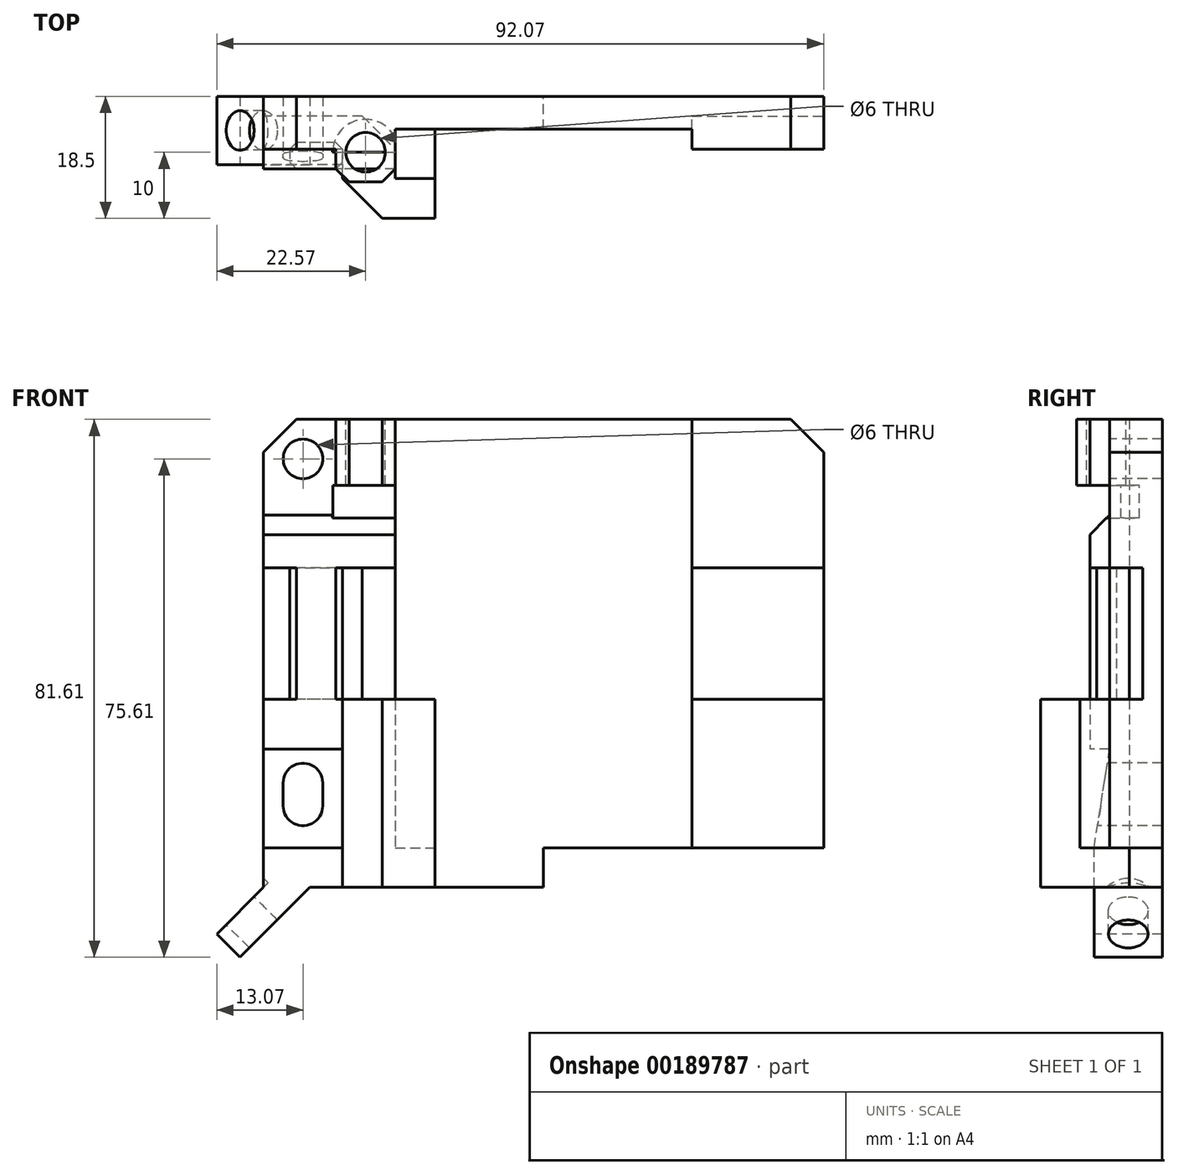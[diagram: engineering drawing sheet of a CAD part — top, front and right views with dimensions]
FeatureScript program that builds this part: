
annotation { "Feature Type Name" : "Feature", "Feature Type Description" : "" }
export const myFeature = defineFeature(function(context is Context, id is Id, definition is map)
    precondition{}
    {
        {
            var Q0;
            Q0=qCreatedBy(makeId("Front.planeOp"),FACE);
            var sketch = newSketch(context, id + "F0", { "sketchPlane" : qUnion([Q0])});
            skLineSegment(sketch, "E0.bottom", {"start": v(42.5, -32.5) * mm, "end": v(-42.5, -32.5) * mm});
            skLineSegment(sketch, "E0.top", {"start": v(42.5, 32.5) * mm, "end": v(-42.5, 32.5) * mm});
            skLineSegment(sketch, "E0.left", {"start": v(42.5, -32.5) * mm, "end": v(42.5, 32.5) * mm});
            skLineSegment(sketch, "E0.right", {"start": v(-42.5, -32.5) * mm, "end": v(-42.5, 32.5) * mm});
            skPoint(sketch, "E0.middle", {"position": v(0, 0) * mm});
            skSolve(sketch);
        }
        {
            var Q0;
            Q0 = qSketchRegion(id + "F0", true);
            extrude(context, id + "F1", {"entities" : qUnion([Q0]), "depth" : 8 * mm});
        }
        {
            var Q0;
            Q0=makeQuery(id+"F1.opExtrude","SWEPT_FACE",FACE,{"disambiguationData":[OSD([sQuery(id+"F0.wireOp",EDGE,"E0.right")])]});
            var sketch = newSketch(context, id + "F2", { "sketchPlane" : qUnion([Q0])});
            skLineSegment(sketch, "E1", {"start": v(8, -32.5) * mm, "end": v(10.38, -32.5) * mm});
            skLineSegment(sketch, "E2", {"start": v(10.38, -32.5) * mm, "end": v(8, -17.5) * mm});
            skLineSegment(sketch, "E3", {"start": v(8, -17.5) * mm, "end": v(8, -32.5) * mm});
            skSolve(sketch);
        }
        {
            var Q0;
            Q0=makeQuery(id+"F1.opExtrude","CAP_FACE",FACE,{"disambiguationData":[OSD([sQuery(id+"F0.wireOp",EDGE,"E0.bottom"),sQuery(id+"F0.wireOp",EDGE,"E0.top"),sQuery(id+"F0.wireOp",EDGE,"E0.left"),sQuery(id+"F0.wireOp",EDGE,"E0.right")])],"isStart":false});
            var sketch = newSketch(context, id + "F3", { "sketchPlane" : qUnion([Q0])});
            skLineSegment(sketch, "E4", {"start": v(-42.5, 26.5) * mm, "end": v(42.5, 26.5) * mm, "construction": true});
            skCircle(sketch, "E5", {"center": v(-36.5, 26.5) * mm, "radius": 3 * mm});
            skLineSegment(sketch, "E6", {"start": v(-36.5, 26.5) * mm, "end": v(-36.5, -32.5) * mm, "construction": true});
            skArc(sketch, "E7", {"start": v(-33.5, -22.65) * mm, "mid": v(-36.5, -19.65) * mm, "end": v(-39.5, -22.65) * mm});
            skArc(sketch, "E8", {"start": v(-39.5, -26.15) * mm, "mid": v(-36.5, -29.15) * mm, "end": v(-33.5, -26.15) * mm});
            skLineSegment(sketch, "E9", {"start": v(-39.5, -26.15) * mm, "end": v(-39.5, -22.65) * mm});
            skLineSegment(sketch, "E10", {"start": v(-33.5, -22.65) * mm, "end": v(-33.5, -26.15) * mm});
            skSolve(sketch);
        }
        {
            var Q0;
            Q0 = qSketchRegion(id + "F2", true);
            extrude(context, id + "F4", {"entities" : qUnion([Q0]), "operationType" : NewBodyOperationType.ADD, "oppositeDirection" : true, "depth" : 12 * mm});
        }
        {
            var Q0;
            Q0 = qSketchRegion(id + "F3", true);
            extrude(context, id + "F5", {"entities" : qUnion([Q0]), "operationType" : NewBodyOperationType.REMOVE, "endBound" : BoundingType.SYMMETRIC, "oppositeDirection" : true, "depth" : 50 * mm});
        }
        {
            var Q0;
            Q0=makeQuery(id+"F1.opExtrude","CAP_FACE",FACE,{"disambiguationData":[OSD([sQuery(id+"F0.wireOp",EDGE,"E0.bottom"),sQuery(id+"F0.wireOp",EDGE,"E0.top"),sQuery(id+"F0.wireOp",EDGE,"E0.left"),sQuery(id+"F0.wireOp",EDGE,"E0.right")])],"isStart":false});
            var sketch = newSketch(context, id + "F6", { "sketchPlane" : qUnion([Q0])});
            skLineSegment(sketch, "E11", {"start": v(-42.5, 10) * mm, "end": v(42.5, 10) * mm});
            skLineSegment(sketch, "E12", {"start": v(42.5, 10) * mm, "end": v(42.5, -10) * mm});
            skLineSegment(sketch, "E13", {"start": v(42.5, -10) * mm, "end": v(-42.5, -10) * mm});
            skLineSegment(sketch, "E14", {"start": v(-42.5, -10) * mm, "end": v(-42.5, 10) * mm});
            skSolve(sketch);
        }
        {
            var Q0;
            Q0 = qSketchRegion(id + "F6", true);
            extrude(context, id + "F7", {"entities" : qUnion([Q0]), "operationType" : NewBodyOperationType.REMOVE, "oppositeDirection" : true, "depth" : 5 * mm});
        }
        {
            var Q0;
            {var subQ0=sQuery(id+"F2.wireOp",EDGE,"E1");Q0=makeQuery(id+"FlQiG0HdQTh74tr_1.1.F4.boolean.opBoolean","MERGE",FACE,{"derivedFrom":[makeQuery(id+"F4.boolean.opBoolean","MERGE",FACE,{"derivedFrom":[makeQuery(id+"F1.opExtrude","SWEPT_FACE",FACE,{"disambiguationData":[OSD([sQuery(id+"F0.wireOp",EDGE,"E0.bottom")])]}),makeQuery(id+"F4.opExtrude","SWEPT_FACE",FACE,{"disambiguationData":[OSD([subQ0])]})]}),makeQuery(id+"FlQiG0HdQTh74tr_1.1.F4.opExtrude","SWEPT_FACE",FACE,{"disambiguationData":[OSD([subQ0])]})]});}
            var sketch = newSketch(context, id + "F8", { "sketchPlane" : qUnion([Q0])});
            skLineSegment(sketch, "E15", {"start": v(-22.5, 8) * mm, "end": v(-22.5, 12.5) * mm});
            skLineSegment(sketch, "E16", {"start": v(-22.5, 12.5) * mm, "end": v(-16.5, 12.5) * mm});
            skLineSegment(sketch, "E17", {"start": v(-16.5, 12.5) * mm, "end": v(-16.5, 18.5) * mm});
            skLineSegment(sketch, "E18", {"start": v(-16.5, 18.5) * mm, "end": v(-30.5, 18.5) * mm});
            skLineSegment(sketch, "E19", {"start": v(-30.5, 18.5) * mm, "end": v(-30.5, 8) * mm});
            skLineSegment(sketch, "E20", {"start": v(-30.5, 8) * mm, "end": v(-22.5, 8) * mm});
            skSolve(sketch);
        }
        {
            var Q0;
            Q0 = qSketchRegion(id + "F8", true);
            extrude(context, id + "F9", {"entities" : qUnion([Q0]), "operationType" : NewBodyOperationType.ADD, "oppositeDirection" : true, "depth" : 22.5 * mm});
        }
        {
            var Q0;
            Q0=makeQuery(id+"F9.opExtrude","SWEPT_EDGE",EDGE,{"disambiguationData":[OSD([sQuery(id+"F8.wireOp",EDGE,"E18"),sQuery(id+"F8.wireOp",EDGE,"E19")])]});
            chamfer(context, id + "F10", {"entities" : qUnion([Q0]), "width" : 6 * mm, "tangentPropagation" : true});
        }
        {
            var Q0;
            {var subQ0=sQuery(id+"F2.wireOp",EDGE,"E1");Q0=makeQuery(id+"F9.boolean.opBoolean","MERGE",FACE,{"derivedFrom":[makeQuery(id+"FlQiG0HdQTh74tr_1.1.F4.boolean.opBoolean","MERGE",FACE,{"derivedFrom":[makeQuery(id+"F4.boolean.opBoolean","MERGE",FACE,{"derivedFrom":[makeQuery(id+"F1.opExtrude","SWEPT_FACE",FACE,{"disambiguationData":[OSD([sQuery(id+"F0.wireOp",EDGE,"E0.bottom")])]}),makeQuery(id+"F4.opExtrude","SWEPT_FACE",FACE,{"disambiguationData":[OSD([subQ0])]})]}),makeQuery(id+"FlQiG0HdQTh74tr_1.1.F4.opExtrude","SWEPT_FACE",FACE,{"disambiguationData":[OSD([subQ0])]})]}),makeQuery(id+"F9.opExtrude","CAP_FACE",FACE,{"disambiguationData":[OSD([sQuery(id+"F8.wireOp",EDGE,"E15"),sQuery(id+"F8.wireOp",EDGE,"E16"),sQuery(id+"F8.wireOp",EDGE,"E17"),sQuery(id+"F8.wireOp",EDGE,"E18"),sQuery(id+"F8.wireOp",EDGE,"E19"),sQuery(id+"F8.wireOp",EDGE,"E20")])],"isStart":true})]});}
            var sketch = newSketch(context, id + "F11", { "sketchPlane" : qUnion([Q0])});
            skLineSegment(sketch, "E21", {"start": v(0, 0) * mm, "end": v(-42.5, 0) * mm});
            skLineSegment(sketch, "E22", {"start": v(-42.5, 0) * mm, "end": v(-42.5, 10.38) * mm});
            skLineSegment(sketch, "E23", {"start": v(-42.5, 10.38) * mm, "end": v(-30.5, 10.38) * mm});
            skLineSegment(sketch, "E24", {"start": v(-30.5, 10.38) * mm, "end": v(-30.5, 12.5) * mm});
            skLineSegment(sketch, "E25", {"start": v(-30.5, 12.5) * mm, "end": v(-24.5, 18.5) * mm});
            skLineSegment(sketch, "E26", {"start": v(-24.5, 18.5) * mm, "end": v(-16.5, 18.5) * mm});
            skLineSegment(sketch, "E27", {"start": v(-16.5, 18.5) * mm, "end": v(-16.5, 8) * mm});
            skLineSegment(sketch, "E28", {"start": v(-16.5, 8) * mm, "end": v(0, 8) * mm});
            skLineSegment(sketch, "E29", {"start": v(0, 8) * mm, "end": v(0, 0) * mm});
            skSolve(sketch);
        }
        {
            var Q0;
            Q0 = qSketchRegion(id + "F11", true);
            extrude(context, id + "F12", {"entities" : qUnion([Q0]), "operationType" : NewBodyOperationType.ADD, "depth" : 6 * mm});
        }
        {
            var Q0;
            Q0=makeQuery(id+"F12.opExtrude","SWEPT_FACE",FACE,{"disambiguationData":[OSD([sQuery(id+"F11.wireOp",EDGE,"E23")])]});
            var sketch = newSketch(context, id + "F13", { "sketchPlane" : qUnion([Q0])});
            skLineSegment(sketch, "E30", {"start": v(-42.5, -38.5) * mm, "end": v(-49.57, -45.57) * mm});
            skLineSegment(sketch, "E31", {"start": v(-49.57, -45.57) * mm, "end": v(-46.04, -49.1) * mm});
            skLineSegment(sketch, "E32", {"start": v(-46.04, -49.1) * mm, "end": v(-35.43, -38.5) * mm});
            skLineSegment(sketch, "E33", {"start": v(-42.5, -38.5) * mm, "end": v(-35.43, -38.5) * mm});
            skSolve(sketch);
        }
        {
            var Q0;
            Q0 = qSketchRegion(id + "F13", true);
            var Q1;
            {var subQ0=sQuery(id+"F11.wireOp",EDGE,"E21");Q1=makeQuery(id+"F7ITQVTQZvwDfWv_1.1.F12.boolean.opBoolean","MERGE",FACE,{"derivedFrom":[makeQuery(id+"F12.boolean.opBoolean","MERGE",FACE,{"derivedFrom":[makeQuery(id+"F1.opExtrude","CAP_FACE",FACE,{"disambiguationData":[OSD([sQuery(id+"F0.wireOp",EDGE,"E0.bottom"),sQuery(id+"F0.wireOp",EDGE,"E0.top"),sQuery(id+"F0.wireOp",EDGE,"E0.left"),sQuery(id+"F0.wireOp",EDGE,"E0.right")])],"isStart":true}),makeQuery(id+"F12.opExtrude","SWEPT_FACE",FACE,{"disambiguationData":[OSD([subQ0])]})]}),makeQuery(id+"F7ITQVTQZvwDfWv_1.1.F12.opExtrude","SWEPT_FACE",FACE,{"disambiguationData":[OSD([subQ0])]})]});}
            extrude(context, id + "F14", {"entities" : qUnion([Q0]), "operationType" : NewBodyOperationType.ADD, "endBound" : BoundingType.UP_TO_SURFACE, "oppositeDirection" : true, "endBoundEntityFace" : qUnion([Q1]), "depth" : 25 * mm});
        }
        {
            var Q0;
            Q0=makeQuery(id+"F14.opExtrude","SWEPT_FACE",FACE,{"disambiguationData":[OSD([sQuery(id+"F13.wireOp",EDGE,"E30")])]});
            var sketch = newSketch(context, id + "F15", { "sketchPlane" : qUnion([Q0])});
            skLineSegment(sketch, "E34", {"start": v(0, -57.28) * mm, "end": v(10.38, -67.28) * mm, "construction": true});
            skLineSegment(sketch, "E35", {"start": v(0, -67.28) * mm, "end": v(10.38, -57.28) * mm, "construction": true});
            skCircle(sketch, "E36", {"center": v(5.19, -62.28) * mm, "radius": 3 * mm});
            skSolve(sketch);
        }
        {
            var Q0;
            Q0 = qSketchRegion(id + "F15", true);
            extrude(context, id + "F16", {"entities" : qUnion([Q0]), "operationType" : NewBodyOperationType.REMOVE, "oppositeDirection" : true, "depth" : 25 * mm});
        }
        {
            var Q0;
            Q0=makeQuery(id+"F14.opExtrude","SWEPT_FACE",FACE,{"disambiguationData":[OSD([sQuery(id+"F13.wireOp",EDGE,"E30")])]});
            var sketch = newSketch(context, id + "F17", { "sketchPlane" : qUnion([Q0])});
            skCircle(sketch, "E37", {"center": v(5.19, -62.28) * mm, "radius": 6 * mm});
            skSolve(sketch);
        }
        {
            var Q0;
            Q0 = qSketchRegion(id + "F17", true);
            extrude(context, id + "F18", {"entities" : qUnion([Q0]), "operationType" : NewBodyOperationType.REMOVE, "depth" : 25 * mm});
        }
        {
            var Q0;
            Q0=makeQuery(id+"F1.opExtrude","SWEPT_EDGE",EDGE,{"disambiguationData":[OSD([sQuery(id+"F0.wireOp",EDGE,"E0.top"),sQuery(id+"F0.wireOp",EDGE,"E0.right")])]});
            var Q1;
            Q1=makeQuery(id+"F1.opExtrude","SWEPT_EDGE",EDGE,{"disambiguationData":[OSD([sQuery(id+"F0.wireOp",EDGE,"E0.top"),sQuery(id+"F0.wireOp",EDGE,"E0.left")])]});
            chamfer(context, id + "F19", {"entities" : qUnion([Q0, Q1]), "width" : 5 * mm, "tangentPropagation" : true});
        }
        {
            var Q0;
            Q0=makeQuery(id+"F12.boolean.opBoolean","MERGE",FACE,{"derivedFrom":[makeQuery(id+"F4.boolean.opBoolean","MERGE",FACE,{"derivedFrom":[makeQuery(id+"F1.opExtrude","SWEPT_FACE",FACE,{"disambiguationData":[OSD([sQuery(id+"F0.wireOp",EDGE,"E0.right")])]}),makeQuery(id+"F4.opExtrude","CAP_FACE",FACE,{"disambiguationData":[OSD([sQuery(id+"F2.wireOp",EDGE,"E1"),sQuery(id+"F2.wireOp",EDGE,"E2"),sQuery(id+"F2.wireOp",EDGE,"E3")])],"isStart":true})]}),makeQuery(id+"F12.opExtrude","SWEPT_FACE",FACE,{"disambiguationData":[OSD([sQuery(id+"F11.wireOp",EDGE,"E22")])]})]});
            var sketch = newSketch(context, id + "F20", { "sketchPlane" : qUnion([Q0])});
            skLineSegment(sketch, "E38", {"start": v(3, 10) * mm, "end": v(3, 15) * mm});
            skLineSegment(sketch, "E39", {"start": v(3, 15) * mm, "end": v(8, 10) * mm});
            skLineSegment(sketch, "E40", {"start": v(8, 10) * mm, "end": v(3, 10) * mm});
            skLineSegment(sketch, "E41", {"start": v(3, -10) * mm, "end": v(3, -15) * mm});
            skLineSegment(sketch, "E42", {"start": v(3, -15) * mm, "end": v(8, -10) * mm});
            skLineSegment(sketch, "E43", {"start": v(8, -10) * mm, "end": v(3, -10) * mm});
            skSolve(sketch);
        }
        {
            var Q0;
            {var subQ0=sQuery(id+"F20.wireOp",EDGE,"E41");var subQ1=sQuery(id+"F20.wireOp",EDGE,"E38");Q0=makeQuery(id+"Fd2kxHlCVzSUctG_1.1.FAOCSB0FVr9LMXz_1.boolean.opBoolean","MERGE",FACE,{"derivedFrom":[makeQuery(id+"FAOCSB0FVr9LMXz_1.boolean.opBoolean","MERGE",FACE,{"derivedFrom":[makeQuery(id+"F7.boolean.opBoolean","COPY",FACE,{"derivedFrom":makeQuery(id+"F7.opExtrude","CAP_FACE",FACE,{"disambiguationData":[OSD([sQuery(id+"F6.wireOp",EDGE,"E11"),sQuery(id+"F6.wireOp",EDGE,"E12"),sQuery(id+"F6.wireOp",EDGE,"E13"),sQuery(id+"F6.wireOp",EDGE,"E14")])],"isStart":false})}),makeQuery(id+"FAOCSB0FVr9LMXz_1.opExtrude","SWEPT_FACE",FACE,{"disambiguationData":[OSD([subQ1])]}),makeQuery(id+"FAOCSB0FVr9LMXz_1.opExtrude","SWEPT_FACE",FACE,{"disambiguationData":[OSD([subQ0])]})]}),makeQuery(id+"Fd2kxHlCVzSUctG_1.1.FAOCSB0FVr9LMXz_1.opExtrude","SWEPT_FACE",FACE,{"disambiguationData":[OSD([subQ1])]}),makeQuery(id+"Fd2kxHlCVzSUctG_1.1.FAOCSB0FVr9LMXz_1.opExtrude","SWEPT_FACE",FACE,{"disambiguationData":[OSD([subQ0])]})]});}
            var sketch = newSketch(context, id + "F21", { "sketchPlane" : qUnion([Q0])});
            skLineSegment(sketch, "E44.bottom", {"start": v(-22.5, -10) * mm, "end": v(22.5, -10) * mm});
            skLineSegment(sketch, "E44.top", {"start": v(-22.5, 10) * mm, "end": v(22.5, 10) * mm});
            skLineSegment(sketch, "E44.left", {"start": v(-22.5, -10) * mm, "end": v(-22.5, 10) * mm});
            skLineSegment(sketch, "E44.right", {"start": v(22.5, -10) * mm, "end": v(22.5, 10) * mm});
            skSolve(sketch);
        }
        {
            var Q0;
            Q0 = qSketchRegion(id + "F21", true);
            extrude(context, id + "F22", {"entities" : qUnion([Q0]), "operationType" : NewBodyOperationType.ADD, "depth" : 5 * mm});
        }
        {
            var Q0;
            Q0=makeQuery(id+"F22.boolean.opBoolean","MERGE",FACE,{"derivedFrom":[makeQuery(id+"FAOCSB0FVr9LMXz_1.boolean.opBoolean","COPY",FACE,{"derivedFrom":makeQuery(id+"FAOCSB0FVr9LMXz_1.opExtrude","CAP_FACE",FACE,{"disambiguationData":[OSD([sQuery(id+"F20.wireOp",EDGE,"E38"),sQuery(id+"F20.wireOp",EDGE,"E39"),sQuery(id+"F20.wireOp",EDGE,"E40")])],"isStart":false})}),makeQuery(id+"FAOCSB0FVr9LMXz_1.boolean.opBoolean","COPY",FACE,{"derivedFrom":makeQuery(id+"FAOCSB0FVr9LMXz_1.opExtrude","CAP_FACE",FACE,{"disambiguationData":[OSD([sQuery(id+"F20.wireOp",EDGE,"E41"),sQuery(id+"F20.wireOp",EDGE,"E42"),sQuery(id+"F20.wireOp",EDGE,"E43")])],"isStart":false})}),makeQuery(id+"F22.opExtrude","SWEPT_FACE",FACE,{"disambiguationData":[OSD([sQuery(id+"F21.wireOp",EDGE,"E44.left")])]})]});
            var sketch = newSketch(context, id + "F23", { "sketchPlane" : qUnion([Q0])});
            skLineSegment(sketch, "E45", {"start": v(3, 0) * mm, "end": v(8, 0) * mm, "construction": true});
            skCircle(sketch, "E46", {"center": v(5.5, 0) * mm, "radius": 2 * mm});
            skSolve(sketch);
        }
        {
            var Q0;
            Q0=makeQuery(id+"F12.boolean.opBoolean","MERGE",FACE,{"derivedFrom":[makeQuery(id+"F4.boolean.opBoolean","MERGE",FACE,{"derivedFrom":[makeQuery(id+"F1.opExtrude","SWEPT_FACE",FACE,{"disambiguationData":[OSD([sQuery(id+"F0.wireOp",EDGE,"E0.right")])]}),makeQuery(id+"F4.opExtrude","CAP_FACE",FACE,{"disambiguationData":[OSD([sQuery(id+"F2.wireOp",EDGE,"E1"),sQuery(id+"F2.wireOp",EDGE,"E2"),sQuery(id+"F2.wireOp",EDGE,"E3")])],"isStart":true})]}),makeQuery(id+"F12.opExtrude","SWEPT_FACE",FACE,{"disambiguationData":[OSD([sQuery(id+"F11.wireOp",EDGE,"E22")])]})]});
            var sketch = newSketch(context, id + "F24", { "sketchPlane" : qUnion([Q0])});
            skLineSegment(sketch, "E47.bottom", {"start": v(8, 10) * mm, "end": v(11, 10) * mm});
            skLineSegment(sketch, "E47.top", {"start": v(8, 18) * mm, "end": v(11, 18) * mm});
            skLineSegment(sketch, "E47.left", {"start": v(8, 10) * mm, "end": v(8, 18) * mm});
            skLineSegment(sketch, "E47.right", {"start": v(11, 10) * mm, "end": v(11, 18) * mm});
            skLineSegment(sketch, "E48.bottom", {"start": v(8, -10) * mm, "end": v(11, -10) * mm});
            skLineSegment(sketch, "E48.top", {"start": v(8, -17.5) * mm, "end": v(11, -17.5) * mm});
            skLineSegment(sketch, "E48.left", {"start": v(8, -10) * mm, "end": v(8, -17.5) * mm});
            skLineSegment(sketch, "E48.right", {"start": v(11, -10) * mm, "end": v(11, -17.5) * mm});
            skSolve(sketch);
        }
        {
            var Q0;
            Q0 = qSketchRegion(id + "F24", true);
            extrude(context, id + "F25", {"entities" : qUnion([Q0]), "operationType" : NewBodyOperationType.ADD, "oppositeDirection" : true, "depth" : 20 * mm});
        }
        {
            var Q0;
            Q0=makeQuery(id+"F25.opExtrude","SWEPT_EDGE",EDGE,{"disambiguationData":[OSD([sQuery(id+"F24.wireOp",EDGE,"E47.top"),sQuery(id+"F24.wireOp",EDGE,"E47.right")])]});
            chamfer(context, id + "F26", {"entities" : qUnion([Q0]), "width" : 3 * mm, "tangentPropagation" : true});
        }
        {
            var Q0;
            Q0=makeQuery(id+"F25.opExtrude","SWEPT_FACE",FACE,{"disambiguationData":[OSD([sQuery(id+"F24.wireOp",EDGE,"E48.right")])]});
            var sketch = newSketch(context, id + "F27", { "sketchPlane" : qUnion([Q0])});
            skLineSegment(sketch, "E49.bottom", {"start": v(-30.5, -10) * mm, "end": v(-38.5, -10) * mm});
            skLineSegment(sketch, "E49.top", {"start": v(-30.5, 10) * mm, "end": v(-38.5, 10) * mm});
            skLineSegment(sketch, "E49.left", {"start": v(-30.5, -10) * mm, "end": v(-30.5, 10) * mm});
            skLineSegment(sketch, "E49.right", {"start": v(-38.5, -10) * mm, "end": v(-38.5, 10) * mm});
            skSolve(sketch);
        }
        {
            var Q0;
            Q0 = qSketchRegion(id + "F27", true);
            extrude(context, id + "F28", {"entities" : qUnion([Q0]), "operationType" : NewBodyOperationType.ADD, "oppositeDirection" : true, "depth" : 4 * mm});
        }
        {
            var Q0;
            Q0=makeQuery(id+"F28.opExtrude","CAP_EDGE",EDGE,{"disambiguationData":[OSD([sQuery(id+"F27.wireOp",EDGE,"E49.left")])],"isStart":true});
            var Q1;
            Q1=makeQuery(id+"F28.opExtrude","CAP_EDGE",EDGE,{"disambiguationData":[OSD([sQuery(id+"F27.wireOp",EDGE,"E49.left")])],"isStart":false});
            var Q2;
            Q2=makeQuery(id+"F28.opExtrude","CAP_EDGE",EDGE,{"disambiguationData":[OSD([sQuery(id+"F27.wireOp",EDGE,"E49.right")])],"isStart":true});
            var Q3;
            Q3=makeQuery(id+"F28.opExtrude","CAP_EDGE",EDGE,{"disambiguationData":[OSD([sQuery(id+"F27.wireOp",EDGE,"E49.right")])],"isStart":false});
            chamfer(context, id + "F29", {"entities" : qUnion([Q0, Q1, Q2, Q3]), "width" : 1 * mm, "tangentPropagation" : true});
        }
        {
            var Q0;
            Q0=makeQuery(id+"F22.opExtrude","CAP_EDGE",EDGE,{"disambiguationData":[OSD([sQuery(id+"F21.wireOp",EDGE,"E44.left")])],"isStart":true});
            var Q1;
            Q1=makeQuery(id+"F22.opExtrude","CAP_EDGE",EDGE,{"disambiguationData":[OSD([sQuery(id+"F21.wireOp",EDGE,"E44.right")])],"isStart":true});
            chamfer(context, id + "F30", {"entities" : qUnion([Q0, Q1]), "width" : 5 * mm, "tangentPropagation" : true});
        }
        {
            var Q0;
            {var subQ4=sQuery(id+"F0.wireOp",EDGE,"E0.right");var subQ6=sQuery(id+"F0.wireOp",EDGE,"E0.left");var subQ8=sQuery(id+"F0.wireOp",EDGE,"E0.top");var subQ11=sQuery(id+"F0.wireOp",EDGE,"E0.bottom");var subQ12=makeQuery(id+"F1.opExtrude","CAP_FACE",FACE,{"disambiguationData":[OSD([subQ11,subQ8,subQ6,subQ4])],"isStart":false});var subQ13=sQuery(id+"F11.wireOp",EDGE,"E28");var subQ29=makeQuery(id+"F1.opExtrude","SWEPT_FACE",FACE,{"disambiguationData":[OSD([subQ11])]});Q0=makeQuery(id+"F22.boolean.opBoolean","MERGE",FACE,{"derivedFrom":[makeQuery(id+"F7ITQVTQZvwDfWv_1.1.F12.boolean.opBoolean","MERGE",FACE,{"derivedFrom":[makeQuery(id+"F7ITQVTQZvwDfWv_1.1.F9.boolean.opBoolean","SPLIT",FACE,{"disambiguationData":[TD([subQ29])],"derivedFrom":makeQuery(id+"F12.boolean.opBoolean","MERGE",FACE,{"derivedFrom":[makeQuery(id+"F9.boolean.opBoolean","SPLIT",FACE,{"disambiguationData":[TD([subQ29])],"derivedFrom":makeQuery(id+"F7.boolean.opBoolean","SPLIT",FACE,{"disambiguationData":[TD([subQ29])],"derivedFrom":subQ12})}),makeQuery(id+"F12.opExtrude","SWEPT_FACE",FACE,{"disambiguationData":[OSD([subQ13])]})]})}),makeQuery(id+"F7ITQVTQZvwDfWv_1.1.F12.opExtrude","SWEPT_FACE",FACE,{"disambiguationData":[OSD([subQ13])]})]}),makeQuery(id+"F7.boolean.opBoolean","SPLIT",FACE,{"disambiguationData":[TD([makeQuery(id+"F1.opExtrude","SWEPT_FACE",FACE,{"disambiguationData":[OSD([subQ8])]})])],"derivedFrom":subQ12}),makeQuery(id+"F22.opExtrude","CAP_FACE",FACE,{"disambiguationData":[OSD([sQuery(id+"F21.wireOp",EDGE,"E44.bottom"),sQuery(id+"F21.wireOp",EDGE,"E44.top"),sQuery(id+"F21.wireOp",EDGE,"E44.left"),sQuery(id+"F21.wireOp",EDGE,"E44.right")])],"isStart":false})]});}
            var sketch = newSketch(context, id + "F31", { "sketchPlane" : qUnion([Q0])});
            skLineSegment(sketch, "E50.bottom", {"start": v(-22.5, 32.5) * mm, "end": v(22.5, 32.5) * mm});
            skLineSegment(sketch, "E50.top", {"start": v(-22.5, -32.5) * mm, "end": v(-16.5, -32.5) * mm});
            skLineSegment(sketch, "E50.left", {"start": v(-22.5, 32.5) * mm, "end": v(-22.5, -32.5) * mm});
            skLineSegment(sketch, "E50.right", {"start": v(22.5, 32.5) * mm, "end": v(22.5, -32.5) * mm});
            skLineSegment(sketch, "E51.bottom", {"start": v(-16.5, -38.5) * mm, "end": v(16.5, -38.5) * mm});
            skLineSegment(sketch, "E51.top", {"start": v(-16.5, -32.5) * mm, "end": v(16.5, -32.5) * mm, "construction": true});
            skLineSegment(sketch, "E51.left", {"start": v(-16.5, -38.5) * mm, "end": v(-16.5, -32.5) * mm});
            skLineSegment(sketch, "E51.right", {"start": v(16.5, -38.5) * mm, "end": v(16.5, -32.5) * mm});
            skLineSegment(sketch, "E52", {"start": v(16.5, -32.5) * mm, "end": v(22.5, -32.5) * mm});
            skSolve(sketch);
        }
        {
            var Q0;
            Q0 = qSketchRegion(id + "F31", true);
            extrude(context, id + "F32", {"entities" : qUnion([Q0]), "operationType" : NewBodyOperationType.REMOVE, "oppositeDirection" : true, "depth" : 3 * mm});
        }
        {
            var Q0;
            {var subQ4=sQuery(id+"F0.wireOp",EDGE,"E0.top");var subQ5=makeQuery(id+"F1.opExtrude","SWEPT_FACE",FACE,{"disambiguationData":[OSD([subQ4])]});var subQ7=sQuery(id+"F0.wireOp",EDGE,"E0.right");var subQ8=makeQuery(id+"F1.opExtrude","SWEPT_FACE",FACE,{"disambiguationData":[OSD([subQ7])]});var subQ17=sQuery(id+"F0.wireOp",EDGE,"E0.left");var subQ20=sQuery(id+"F0.wireOp",EDGE,"E0.bottom");var subQ21=makeQuery(id+"F1.opExtrude","CAP_FACE",FACE,{"disambiguationData":[OSD([subQ20,subQ4,subQ17,subQ7])],"isStart":false});var subQ22=sQuery(id+"F11.wireOp",EDGE,"E28");var subQ36=makeQuery(id+"F1.opExtrude","SWEPT_FACE",FACE,{"disambiguationData":[OSD([subQ20])]});Q0=makeQuery(id+"F32.boolean.opBoolean","SPLIT",FACE,{"disambiguationData":[TD([subQ8])],"derivedFrom":makeQuery(id+"F22.boolean.opBoolean","MERGE",FACE,{"derivedFrom":[makeQuery(id+"F7ITQVTQZvwDfWv_1.1.F12.boolean.opBoolean","MERGE",FACE,{"derivedFrom":[makeQuery(id+"F7ITQVTQZvwDfWv_1.1.F9.boolean.opBoolean","SPLIT",FACE,{"disambiguationData":[TD([subQ36])],"derivedFrom":makeQuery(id+"F12.boolean.opBoolean","MERGE",FACE,{"derivedFrom":[makeQuery(id+"F9.boolean.opBoolean","SPLIT",FACE,{"disambiguationData":[TD([subQ36])],"derivedFrom":makeQuery(id+"F7.boolean.opBoolean","SPLIT",FACE,{"disambiguationData":[TD([subQ36])],"derivedFrom":subQ21})}),makeQuery(id+"F12.opExtrude","SWEPT_FACE",FACE,{"disambiguationData":[OSD([subQ22])]})]})}),makeQuery(id+"F7ITQVTQZvwDfWv_1.1.F12.opExtrude","SWEPT_FACE",FACE,{"disambiguationData":[OSD([subQ22])]})]}),makeQuery(id+"F7.boolean.opBoolean","SPLIT",FACE,{"disambiguationData":[TD([subQ5])],"derivedFrom":subQ21}),makeQuery(id+"F22.opExtrude","CAP_FACE",FACE,{"disambiguationData":[OSD([sQuery(id+"F21.wireOp",EDGE,"E44.bottom"),sQuery(id+"F21.wireOp",EDGE,"E44.top"),sQuery(id+"F21.wireOp",EDGE,"E44.left"),sQuery(id+"F21.wireOp",EDGE,"E44.right")])],"isStart":false})]})});}
            var sketch = newSketch(context, id + "F33", { "sketchPlane" : qUnion([Q0])});
            skLineSegment(sketch, "E53.bottom", {"start": v(-22.5, 32.5) * mm, "end": v(-31.5, 32.5) * mm});
            skLineSegment(sketch, "E53.top", {"start": v(-22.5, 22.5) * mm, "end": v(-31.5, 22.5) * mm});
            skLineSegment(sketch, "E53.left", {"start": v(-22.5, 32.5) * mm, "end": v(-22.5, 22.5) * mm});
            skLineSegment(sketch, "E53.right", {"start": v(-31.5, 32.5) * mm, "end": v(-31.5, 22.5) * mm});
            skCircle(sketch, "E54", {"center": v(-36.5, 26.5) * mm, "radius": 5 * mm, "construction": true});
            skSolve(sketch);
        }
        {
            var Q0;
            Q0 = qSketchRegion(id + "F33", true);
            extrude(context, id + "F34", {"entities" : qUnion([Q0]), "operationType" : NewBodyOperationType.ADD, "depth" : 5 * mm});
        }
        {
            var Q0;
            Q0=makeQuery(id+"F34.boolean.opBoolean","MERGE",FACE,{"derivedFrom":[makeQuery(id+"F1.opExtrude","SWEPT_FACE",FACE,{"disambiguationData":[OSD([sQuery(id+"F0.wireOp",EDGE,"E0.top")])]}),makeQuery(id+"F34.opExtrude","SWEPT_FACE",FACE,{"disambiguationData":[OSD([sQuery(id+"F33.wireOp",EDGE,"E53.bottom")])]})]});
            var sketch = newSketch(context, id + "F35", { "sketchPlane" : qUnion([Q0])});
            skLineSegment(sketch, "E55", {"start": v(-27, -13) * mm, "end": v(-27, 0) * mm, "construction": true});
            skCircle(sketch, "E56", {"center": v(-27, -8.5) * mm, "radius": 3 * mm});
            skSolve(sketch);
        }
        {
            var Q0;
            Q0 = qSketchRegion(id + "F35", true);
            extrude(context, id + "F36", {"entities" : qUnion([Q0]), "operationType" : NewBodyOperationType.REMOVE, "oppositeDirection" : true, "depth" : 14 * mm});
        }
        {
            var Q0;
            Q0=makeQuery(id+"F34.opExtrude","SWEPT_FACE",FACE,{"disambiguationData":[OSD([sQuery(id+"F33.wireOp",EDGE,"E53.top")])]});
            var sketch = newSketch(context, id + "F37", { "sketchPlane" : qUnion([Q0])});
            skCircle(sketch, "E57", {"center": v(-27, 8.5) * mm, "radius": 5 * mm});
            skSolve(sketch);
        }
        {
            var Q0;
            Q0 = qSketchRegion(id + "F37", true);
            extrude(context, id + "F38", {"entities" : qUnion([Q0]), "operationType" : NewBodyOperationType.REMOVE, "depth" : 5 * mm});
        }
        {
            var Q0;
            Q0=makeQuery(id+"F34.opExtrude","CAP_EDGE",EDGE,{"disambiguationData":[OSD([sQuery(id+"F33.wireOp",EDGE,"E53.right")])],"isStart":false});
            var Q1;
            Q1=makeQuery(id+"F34.opExtrude","CAP_EDGE",EDGE,{"disambiguationData":[OSD([sQuery(id+"F33.wireOp",EDGE,"E53.left")])],"isStart":false});
            chamfer(context, id + "F39", {"entities" : qUnion([Q0, Q1]), "width" : 2 * mm, "tangentPropagation" : true});
        }
    });
